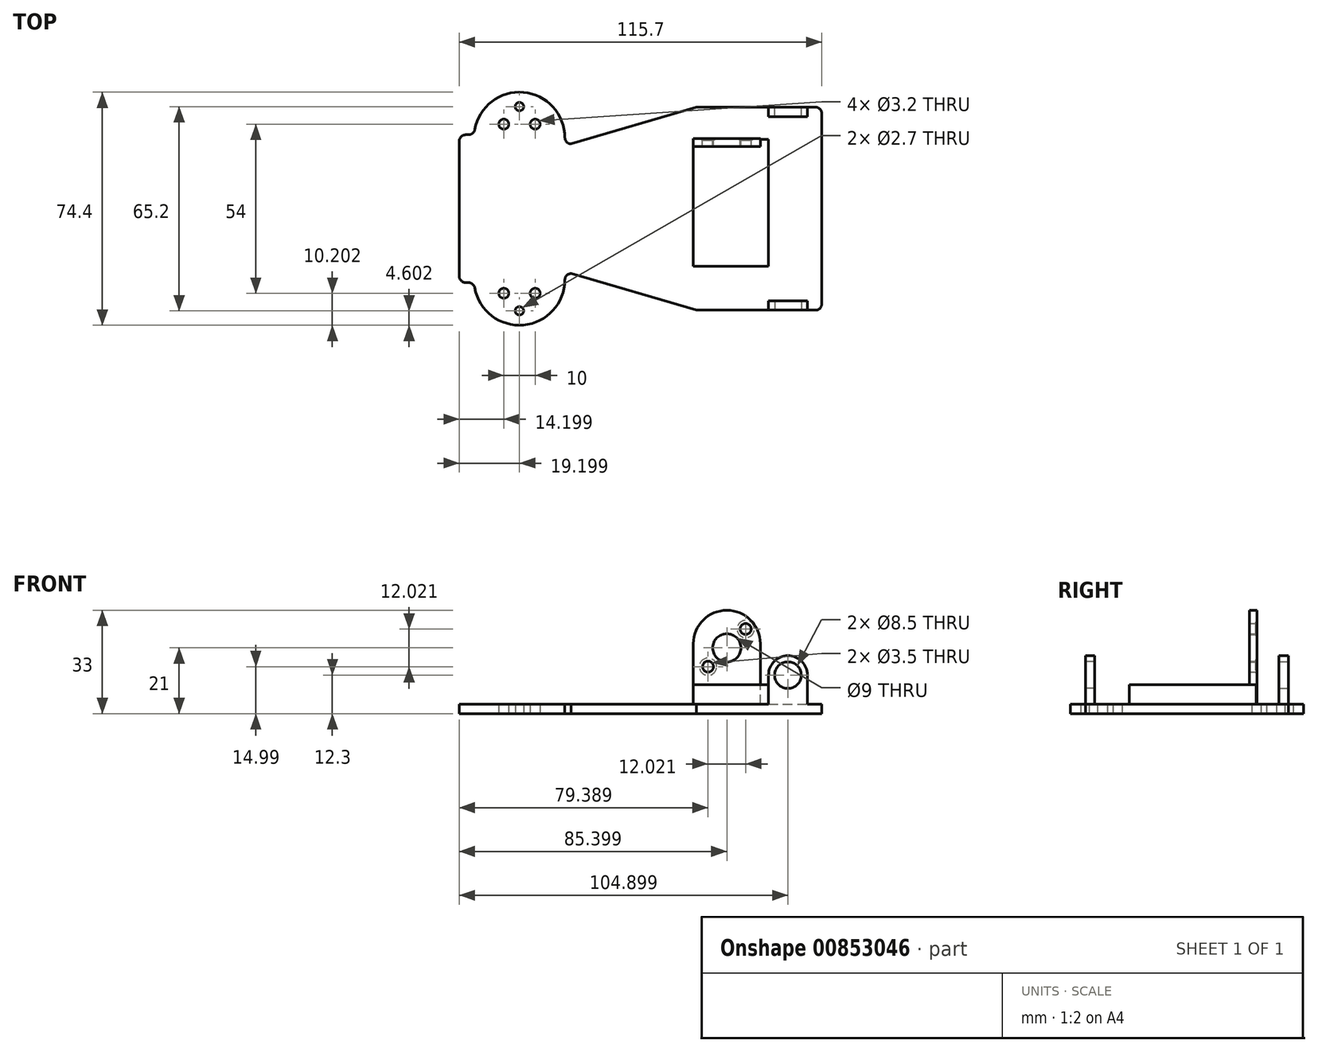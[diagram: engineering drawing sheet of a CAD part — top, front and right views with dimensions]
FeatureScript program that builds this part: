
annotation { "Feature Type Name" : "Feature", "Feature Type Description" : "" }
export const myFeature = defineFeature(function(context is Context, id is Id, definition is map)
    precondition{}
    {
        {
            var Q0;
            Q0=qCreatedBy(makeId("Top.planeOp"),FACE);
            var sketch = newSketch(context, id + "F0", { "sketchPlane" : qUnion([Q0])});
            skLineSegment(sketch, "E0", {"start": v(-197.6, -13.92) * mm, "end": v(73.01, -13.92) * mm});
            skLineSegment(sketch, "E1", {"start": v(-197.6, -13.92) * mm, "end": v(-197.6, 7.68) * mm});
            skLineSegment(sketch, "E2", {"start": v(-195.6, 9.68) * mm, "end": v(-194.63, 9.68) * mm});
            skLineSegment(sketch, "E3", {"start": v(-192.9, 8.78) * mm, "end": v(-163.9, 8.78) * mm});
            skLineSegment(sketch, "E4", {"start": v(-163.9, 8.78) * mm, "end": v(-163.9, 8.78) * mm});
            skArc(sketch, "E5", {"start": v(-163.9, 8.78) * mm, "mid": v(-177.11, 23.23) * mm, "end": v(-192.66, 11.33) * mm});
            skLineSegment(sketch, "E6", {"start": v(-121.9, 18.48) * mm, "end": v(-83.9, 18.48) * mm});
            skLineSegment(sketch, "E7", {"start": v(-81.9, 16.48) * mm, "end": v(-81.9, -22.02) * mm});
            skLineSegment(sketch, "E8.MirrorCS", {"start": v(-197.6, -13.92) * mm, "end": v(-197.6, -35.52) * mm});
            skLineSegment(sketch, "E9.MirrorCS", {"start": v(-195.6, -37.52) * mm, "end": v(-194.63, -37.52) * mm});
            skArc(sketch, "E10.MirrorCS", {"start": v(-163.9, -36.62) * mm, "mid": v(-177.11, -51.06) * mm, "end": v(-192.66, -39.17) * mm});
            skLineSegment(sketch, "E11.MirrorCS", {"start": v(-163.9, -36.62) * mm, "end": v(-163.9, -36.62) * mm});
            skLineSegment(sketch, "E12.MirrorCS", {"start": v(-121.9, -46.32) * mm, "end": v(-83.9, -46.32) * mm});
            skLineSegment(sketch, "E13.MirrorCS", {"start": v(-81.9, -44.32) * mm, "end": v(-81.9, -5.82) * mm});
            skArc(sketch, "E14.filletArc", {"start": v(-163.9, 8.78) * mm, "mid": v(-163.3, 7.37) * mm, "end": v(-161.9, 6.78) * mm});
            skPoint(sketch, "E15.visualSharp", {"position": v(-163.9, -37.52) * mm});
            skArc(sketch, "E15.filletArc", {"start": v(-161.9, -34.62) * mm, "mid": v(-163.3, -35.2) * mm, "end": v(-163.9, -36.62) * mm});
            skPoint(sketch, "E16.visualSharp", {"position": v(-197.6, 9.68) * mm});
            skArc(sketch, "E16.filletArc", {"start": v(-195.6, 9.68) * mm, "mid": v(-197, 9.1) * mm, "end": v(-197.6, 7.68) * mm});
            skPoint(sketch, "E17.visualSharp", {"position": v(-197.6, -37.52) * mm});
            skArc(sketch, "E17.filletArc", {"start": v(-197.6, -35.52) * mm, "mid": v(-197, -36.93) * mm, "end": v(-195.6, -37.52) * mm});
            skPoint(sketch, "E18.visualSharp", {"position": v(-81.9, -46.32) * mm});
            skArc(sketch, "E18.filletArc", {"start": v(-83.9, -46.32) * mm, "mid": v(-82.48, -45.73) * mm, "end": v(-81.9, -44.32) * mm});
            skPoint(sketch, "E19.visualSharp", {"position": v(-81.9, 18.48) * mm});
            skArc(sketch, "E19.filletArc", {"start": v(-81.9, 16.48) * mm, "mid": v(-82.48, 17.9) * mm, "end": v(-83.9, 18.48) * mm});
            skLineSegment(sketch, "E20", {"start": v(-178.4, -59.4) * mm, "end": v(-178.4, 51.77) * mm});
            skCircle(sketch, "E21", {"center": v(-183.4, -40.92) * mm, "radius": 1.6 * mm});
            skCircle(sketch, "E22", {"center": v(-178.4, -46.52) * mm, "radius": 1.35 * mm});
            skCircle(sketch, "E23.MirrorC", {"center": v(-173.4, -40.92) * mm, "radius": 1.6 * mm});
            skCircle(sketch, "E24.MirrorC", {"center": v(-183.4, 13.08) * mm, "radius": 1.6 * mm});
            skCircle(sketch, "E25.MirrorC", {"center": v(-173.4, 13.08) * mm, "radius": 1.6 * mm});
            skCircle(sketch, "E26.MirrorC", {"center": v(-178.4, 18.68) * mm, "radius": 1.35 * mm});
            skLineSegment(sketch, "E27", {"start": v(-101.9, -46.32) * mm, "end": v(-101.9, 18.48) * mm});
            skLineSegment(sketch, "E28", {"start": v(-121.9, -46.32) * mm, "end": v(-121.9, 18.48) * mm});
            skPoint(sketch, "E29.visualSharp", {"position": v(-192.86, -37.52) * mm});
            skArc(sketch, "E29.filletArc", {"start": v(-192.66, -39.17) * mm, "mid": v(-193.35, -37.98) * mm, "end": v(-194.63, -37.52) * mm});
            skArc(sketch, "E30.filletArc", {"start": v(-194.63, 9.68) * mm, "mid": v(-193.35, 10.15) * mm, "end": v(-192.66, 11.33) * mm});
            skLineSegment(sketch, "E31", {"start": v(-161.9, 6.78) * mm, "end": v(-121.9, 18.48) * mm});
            skLineSegment(sketch, "E32", {"start": v(-161.9, -34.62) * mm, "end": v(-121.9, -46.32) * mm});
            skLineSegment(sketch, "E33", {"start": v(-161.9, 6.78) * mm, "end": v(-161.9, -34.62) * mm});
            skSolve(sketch);
        }
        {
            var Q0;
            Q0=qSketchRegion(id+"F0",true);
            extrude(context, id + "F1", {"entities" : qUnion([Q0]), "depth" : 3 * mm, "offsetDistance" : 25 * mm});
        }
        {
            var Q0;
            Q0=qCreatedBy(makeId("Top.planeOp"),FACE);
            var sketch = newSketch(context, id + "F2", { "sketchPlane" : qUnion([Q0])});
            skLineSegment(sketch, "E34.bottom", {"start": v(-86.9, -46.32) * mm, "end": v(-86.9, 18.48) * mm});
            skLineSegment(sketch, "E34.top", {"start": v(-98.9, -46.32) * mm, "end": v(-98.9, -7.32) * mm});
            skLineSegment(sketch, "E34.left", {"start": v(-86.9, -46.32) * mm, "end": v(-98.9, -46.32) * mm});
            skLineSegment(sketch, "E34.right", {"start": v(-86.9, 18.48) * mm, "end": v(-98.9, 18.48) * mm});
            skLineSegment(sketch, "E35", {"start": v(-98.9, -7.32) * mm, "end": v(-122.9, -7.32) * mm});
            skLineSegment(sketch, "E36", {"start": v(-122.9, -7.32) * mm, "end": v(-122.9, 8.48) * mm});
            skLineSegment(sketch, "E37", {"start": v(-122.9, 8.48) * mm, "end": v(-98.9, 8.48) * mm});
            skLineSegment(sketch, "E38.trimOffspring", {"start": v(-98.9, 8.48) * mm, "end": v(-98.9, 18.48) * mm});
            skPoint(sketch, "E39.centerSnap0", {"position": v(-92.9, -46.32) * mm});
            skPoint(sketch, "E40", {"position": v(-98.9, -46.32) * mm});
            skPoint(sketch, "E41", {"position": v(-86.9, -46.32) * mm});
            skPoint(sketch, "E42", {"position": v(-122.9, 8.48) * mm});
            skPoint(sketch, "E43", {"position": v(-86.9, 18.48) * mm});
            skPoint(sketch, "E44", {"position": v(-98.9, 18.48) * mm});
            skSolve(sketch);
        }
        {
            var Q0;
            Q0=qCreatedBy(makeId("Front.planeOp"),FACE);
            var Q1;
            Q1=sQuery(id+"F0.wireOp",VERTEX,"E18.visualSharp");
            cPlane(context, id + "F3", {"entities" : qUnion([Q0, Q1]), "cplaneType" : CPlaneType.PLANE_POINT, "offset" : 25 * mm, "width" : 150 * mm, "height" : 150 * mm});
        }
        {
            var Q0;
            Q0=qCreatedBy(makeId("Front.planeOp"),FACE);
            var Q1;
            Q1=sQuery(id+"F2.wireOp",VERTEX,"E34.right.end");
            cPlane(context, id + "F4", {"entities" : qUnion([Q0, Q1]), "cplaneType" : CPlaneType.PLANE_POINT, "offset" : 25 * mm, "width" : 150 * mm, "height" : 150 * mm});
        }
        {
            var Q0;
            Q0=qCreatedBy(makeId("Front.planeOp"),FACE);
            var Q1;
            Q1=sQuery(id+"F2.wireOp",VERTEX,"E37.end");
            cPlane(context, id + "F5", {"entities" : qUnion([Q0, Q1]), "cplaneType" : CPlaneType.PLANE_POINT, "offset" : 25 * mm, "width" : 150 * mm, "height" : 150 * mm});
        }
        {
            var Q0;
            Q0=qCreatedBy(id+"F3.planeOp",FACE);
            var sketch = newSketch(context, id + "F6", { "sketchPlane" : qUnion([Q0])});
            skLineSegment(sketch, "E45.bottom", {"start": v(-98.9, 0) * mm, "end": v(-86.5, 0) * mm});
            skLineSegment(sketch, "E45.top", {"start": v(-98.9, 12.3) * mm, "end": v(-86.5, 12.3) * mm});
            skLineSegment(sketch, "E45.left", {"start": v(-98.9, 0) * mm, "end": v(-98.9, 12.3) * mm});
            skLineSegment(sketch, "E45.right", {"start": v(-86.5, 0) * mm, "end": v(-86.5, 12.3) * mm});
            skArc(sketch, "E46", {"start": v(-86.5, 12.3) * mm, "mid": v(-92.7, 18.5) * mm, "end": v(-98.9, 12.3) * mm});
            skCircle(sketch, "E47", {"center": v(-92.7, 12.3) * mm, "radius": 4.25 * mm});
            skSolve(sketch);
        }
        {
            var Q0;
            Q0=qSketchRegion(id+"F6",true);
            extrude(context, id + "F7", {"entities" : qUnion([Q0]), "operationType" : NewBodyOperationType.ADD, "oppositeDirection" : true, "depth" : 3 * mm, "offsetDistance" : 25 * mm});
        }
        {
            var Q0;
            Q0=qCreatedBy(id+"F4.planeOp",FACE);
            var sketch = newSketch(context, id + "F8", { "sketchPlane" : qUnion([Q0])});
            skLineSegment(sketch, "E48.bottom", {"start": v(-98.9, 0) * mm, "end": v(-86.5, 0) * mm});
            skLineSegment(sketch, "E48.top", {"start": v(-98.9, 12.3) * mm, "end": v(-86.5, 12.3) * mm});
            skLineSegment(sketch, "E48.left", {"start": v(-98.9, 0) * mm, "end": v(-98.9, 12.3) * mm});
            skLineSegment(sketch, "E48.right", {"start": v(-86.5, 0) * mm, "end": v(-86.5, 12.3) * mm});
            skArc(sketch, "E49", {"start": v(-86.5, 12.3) * mm, "mid": v(-92.7, 18.5) * mm, "end": v(-98.9, 12.3) * mm});
            skCircle(sketch, "E50", {"center": v(-92.7, 12.3) * mm, "radius": 4.25 * mm});
            skSolve(sketch);
        }
        {
            var Q0;
            Q0=qSketchRegion(id+"F8",true);
            extrude(context, id + "F9", {"entities" : qUnion([Q0]), "operationType" : NewBodyOperationType.ADD, "depth" : 3 * mm, "offsetDistance" : 25 * mm});
        }
        {
            var Q0;
            Q0=qCreatedBy(id+"F5.planeOp",FACE);
            var sketch = newSketch(context, id + "F10", { "sketchPlane" : qUnion([Q0])});
            skLineSegment(sketch, "E51.bottom", {"start": v(-122.9, 0) * mm, "end": v(-101.5, 0) * mm});
            skLineSegment(sketch, "E51.top", {"start": v(-122.9, 22.3) * mm, "end": v(-101.5, 22.3) * mm});
            skLineSegment(sketch, "E51.left", {"start": v(-122.9, 0) * mm, "end": v(-122.9, 22.3) * mm});
            skLineSegment(sketch, "E51.right", {"start": v(-101.5, 0) * mm, "end": v(-101.5, 22.3) * mm});
            skArc(sketch, "E52", {"start": v(-101.5, 22.3) * mm, "mid": v(-112.2, 33) * mm, "end": v(-122.9, 22.3) * mm});
            skCircle(sketch, "E53", {"center": v(-112.2, 21) * mm, "radius": 4.5 * mm});
            skPoint(sketch, "E53.centerSnap0", {"position": v(-112.2, 33) * mm});
            skLineSegment(sketch, "E54", {"start": v(-118.2, 27.01) * mm, "end": v(-112.2, 21) * mm});
            skLineSegment(sketch, "E55", {"start": v(-112.2, 33) * mm, "end": v(-112.2, 13.34) * mm});
            skLineSegment(sketch, "E56", {"start": v(-112.2, 21) * mm, "end": v(-120.33, 21) * mm});
            skPoint(sketch, "E57", {"position": v(-118.2, 27.01) * mm});
            skPoint(sketch, "E58", {"position": v(-122.9, 0) * mm});
            skPoint(sketch, "E59.MirrorP", {"position": v(-118.2, 14.99) * mm});
            skPoint(sketch, "E60.MirrorP", {"position": v(-106.18, 27.01) * mm});
            skPoint(sketch, "E61.MirrorP", {"position": v(-106.18, 14.99) * mm});
            skSolve(sketch);
        }
        {
            var Q0;
            Q0=qSketchRegion(id+"F10",true);
            extrude(context, id + "F11", {"entities" : qUnion([Q0]), "operationType" : NewBodyOperationType.ADD, "depth" : 2.5 * mm, "offsetDistance" : 25 * mm});
        }
        {
            var Q0;
            Q0=sQuery(id+"F10.wireOp",VERTEX,"E60.MirrorP");
            var Q1;
            Q1=sQuery(id+"F10.wireOp",VERTEX,"E59.MirrorP");
            var Q2;
            Q2=makeQuery(id+"F1.opExtrude","SWEPT_BODY",BODY,{"disambiguationData":[OSD([sQuery(id+"F0.wireOp",EDGE,"E1"),sQuery(id+"F0.wireOp",EDGE,"E2"),sQuery(id+"F0.wireOp",EDGE,"747f3917-a403-47d7-be17-b1600b637754"),sQuery(id+"F0.wireOp",EDGE,"E4"),sQuery(id+"F0.wireOp",EDGE,"4c9f211f-dca9-4b0b-8b14-96c65f567eb5"),sQuery(id+"F0.wireOp",EDGE,"E5"),sQuery(id+"F0.wireOp",EDGE,"E6"),sQuery(id+"F0.wireOp",EDGE,"E7"),sQuery(id+"F0.wireOp",EDGE,"e2f4631c-2fa2-4fb0-aa32-fbbd06efad87"),sQuery(id+"F0.wireOp",EDGE,"E8.MirrorCS"),sQuery(id+"F0.wireOp",EDGE,"E9.MirrorCS"),sQuery(id+"F0.wireOp",EDGE,"0248994d-1b11-48b6-9ee8-a59c6f9ca753.MirrorCS"),sQuery(id+"F0.wireOp",EDGE,"E10.MirrorCS"),sQuery(id+"F0.wireOp",EDGE,"E11.MirrorCS"),sQuery(id+"F0.wireOp",EDGE,"d53c2d9c-1ec1-4c28-b0a0-111513367524.MirrorCS"),sQuery(id+"F0.wireOp",EDGE,"bffd064e-b9d1-4ec9-8389-047fa968f274.MirrorCS"),sQuery(id+"F0.wireOp",EDGE,"E12.MirrorCS"),sQuery(id+"F0.wireOp",EDGE,"E13.MirrorCS"),sQuery(id+"F0.wireOp",EDGE,"e527b50f-b411-496e-aab0-89e9a39e1ded.filletArc"),sQuery(id+"F0.wireOp",EDGE,"E14.filletArc"),sQuery(id+"F0.wireOp",EDGE,"bd301ba9-1abb-4656-8ab6-7715adf7f377.filletArc"),sQuery(id+"F0.wireOp",EDGE,"E15.filletArc"),sQuery(id+"F0.wireOp",EDGE,"E16.filletArc"),sQuery(id+"F0.wireOp",EDGE,"E17.filletArc"),sQuery(id+"F0.wireOp",EDGE,"E18.filletArc"),sQuery(id+"F0.wireOp",EDGE,"E19.filletArc"),sQuery(id+"F0.wireOp",EDGE,"E21"),sQuery(id+"F0.wireOp",EDGE,"E22"),sQuery(id+"F0.wireOp",EDGE,"E23.MirrorC"),sQuery(id+"F0.wireOp",EDGE,"E24.MirrorC"),sQuery(id+"F0.wireOp",EDGE,"E25.MirrorC"),sQuery(id+"F0.wireOp",EDGE,"E26.MirrorC")])]});
            hole(context, id + "F12", {"style" : HoleStyle.C_SINK, "endStyle" : HoleEndStyle.THROUGH, "oppositeDirection" : true, "holeDiameter" : 3.5 * mm, "cSinkDiameter" : 5.5 * mm, "cSinkAngle" : 120 * degree, "majorDiameter" : 5 * mm, "isTappedThrough" : true, "tappedDepth" : 12 * mm, "tapClearance" : 3, "startFromSketch" : true, "locations" : qUnion([Q0, Q1]), "scope" : qUnion([Q2])});
        }
        {
            var Q0;
            Q0=qCreatedBy(makeId("Front.planeOp"),FACE);
            var Q1;
            Q1=sQuery(id+"F2.wireOp",VERTEX,"E35.end");
            cPlane(context, id + "F13", {"entities" : qUnion([Q0, Q1]), "cplaneType" : CPlaneType.PLANE_POINT, "offset" : 25 * mm, "width" : 150 * mm, "height" : 150 * mm});
        }
        {
            var Q0;
            Q0=qCreatedBy(id+"F13.planeOp",FACE);
            var sketch = newSketch(context, id + "F14", { "sketchPlane" : qUnion([Q0])});
            skLineSegment(sketch, "E62.bottom", {"start": v(-122.9, 0) * mm, "end": v(-98.9, 0) * mm});
            skLineSegment(sketch, "E62.top", {"start": v(-122.9, 9.2) * mm, "end": v(-98.9, 9.2) * mm});
            skLineSegment(sketch, "E62.left", {"start": v(-122.9, 0) * mm, "end": v(-122.9, 9.2) * mm});
            skLineSegment(sketch, "E62.right", {"start": v(-98.9, 0) * mm, "end": v(-98.9, 9.2) * mm});
            skSolve(sketch);
        }
        {
            var Q0;
            Q0=qSketchRegion(id+"F14",true);
            extrude(context, id + "F15", {"entities" : qUnion([Q0]), "operationType" : NewBodyOperationType.ADD, "oppositeDirection" : true, "depth" : 15.5 * mm, "offsetDistance" : 25 * mm});
        }
        {
            var Q0;
            Q0 = qSketchRegion(id + "F14", true);
            extrude(context, id + "F16", {"entities" : qUnion([Q0]), "operationType" : NewBodyOperationType.ADD, "depth" : 25 * mm, "offsetDistance" : 25 * mm});
        }
    });
